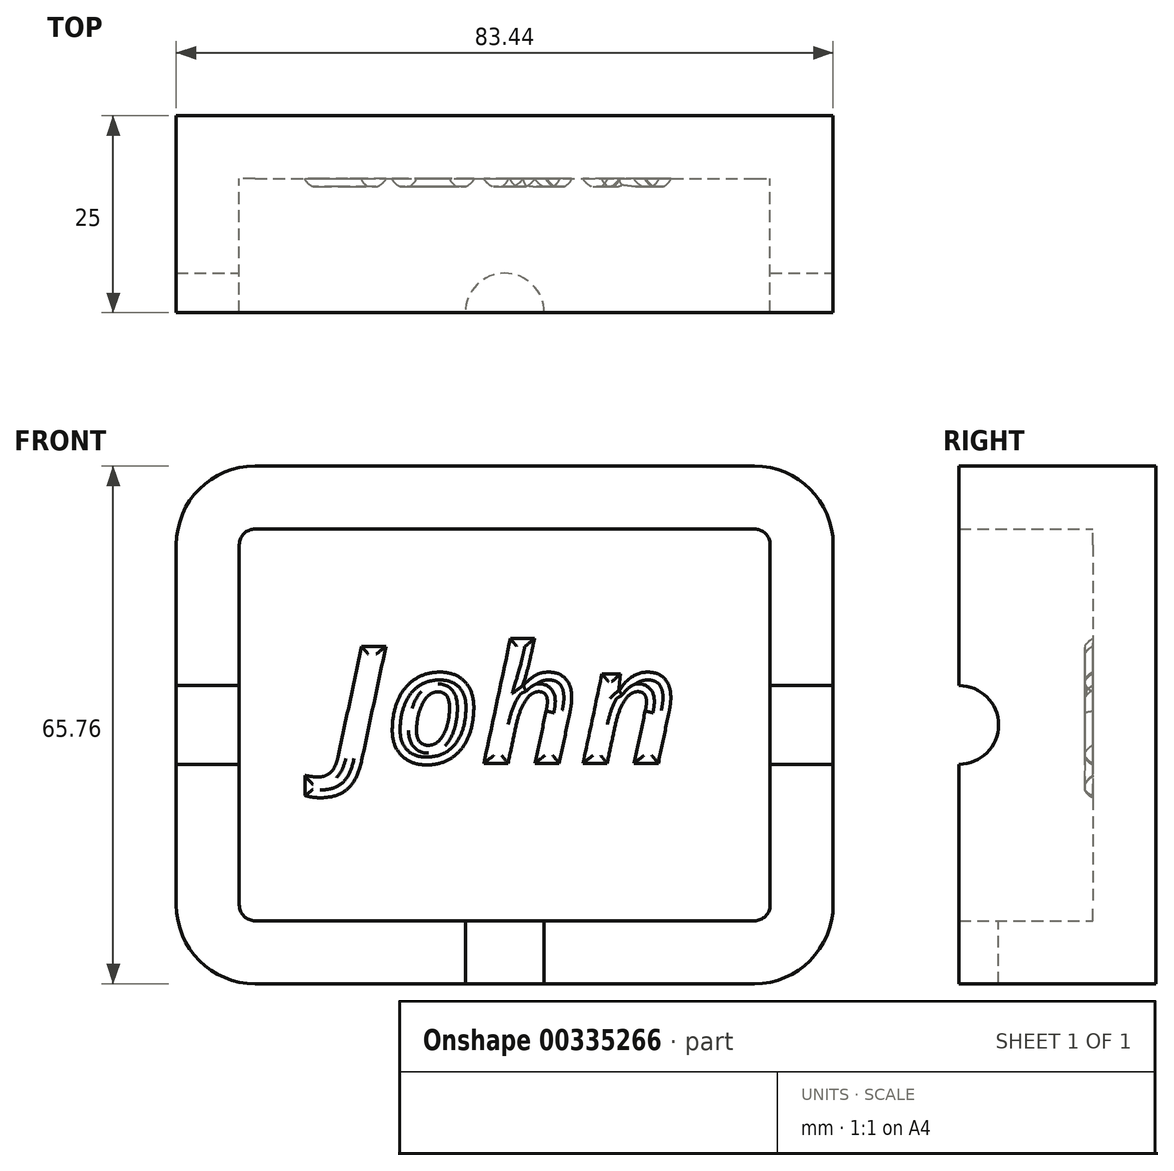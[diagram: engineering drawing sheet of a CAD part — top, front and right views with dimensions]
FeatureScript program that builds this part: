
annotation { "Feature Type Name" : "Feature", "Feature Type Description" : "" }
export const myFeature = defineFeature(function(context is Context, id is Id, definition is map)
    precondition{}
    {
        {
            var Q0;
            Q0=qCreatedBy(makeId("Front.planeOp"),FACE);
            var sketch = newSketch(context, id + "F0", { "sketchPlane" : qUnion([Q0])});
            skLineSegment(sketch, "E0.bottom", {"start": v(-52.7, 43.56) * mm, "end": v(30.74, 43.56) * mm});
            skLineSegment(sketch, "E0.top", {"start": v(-52.7, -22.2) * mm, "end": v(30.74, -22.2) * mm});
            skLineSegment(sketch, "E0.left", {"start": v(-52.7, 43.56) * mm, "end": v(-52.7, -22.2) * mm});
            skLineSegment(sketch, "E0.right", {"start": v(30.74, 43.56) * mm, "end": v(30.74, -22.2) * mm});
            skSolve(sketch);
        }
        {
            var Q0;
            Q0 = qSketchRegion(id + "F0", true);
            extrude(context, id + "F1", {"entities" : qUnion([Q0]), "depth" : 25 * mm});
        }
        {
            var Q0;
            Q0=makeQuery(id+"F1.opExtrude","SWEPT_EDGE",EDGE,{"disambiguationData":[OSD([sQuery(id+"F0.wireOp",EDGE,"E0.bottom"),sQuery(id+"F0.wireOp",EDGE,"E0.right")])]});
            var Q1;
            Q1=makeQuery(id+"F1.opExtrude","SWEPT_EDGE",EDGE,{"disambiguationData":[OSD([sQuery(id+"F0.wireOp",EDGE,"E0.top"),sQuery(id+"F0.wireOp",EDGE,"E0.right")])]});
            var Q2;
            Q2=makeQuery(id+"F1.opExtrude","SWEPT_EDGE",EDGE,{"disambiguationData":[OSD([sQuery(id+"F0.wireOp",EDGE,"E0.bottom"),sQuery(id+"F0.wireOp",EDGE,"E0.left")])]});
            var Q3;
            Q3=makeQuery(id+"F1.opExtrude","SWEPT_EDGE",EDGE,{"disambiguationData":[OSD([sQuery(id+"F0.wireOp",EDGE,"E0.top"),sQuery(id+"F0.wireOp",EDGE,"E0.left")])]});
            fillet(context, id + "F2", {"entities" : qUnion([Q0, Q1, Q2, Q3]), "radius" : 10 * mm, "tangentPropagation" : true, "allowEdgeOverflow" : false});
        }
        {
            var Q0;
            Q0=makeQuery(id+"F1.opExtrude","CAP_FACE",FACE,{"disambiguationData":[OSD([sQuery(id+"F0.wireOp",EDGE,"E0.bottom"),sQuery(id+"F0.wireOp",EDGE,"E0.top"),sQuery(id+"F0.wireOp",EDGE,"E0.left"),sQuery(id+"F0.wireOp",EDGE,"E0.right")])],"isStart":false});
            shell(context, id + "F3", {"entities" : qUnion([Q0]), "thickness" : 8 * mm});
        }
        {
            var Q0;
            Q0=makeQuery(id+"F1.opExtrude","SWEPT_FACE",FACE,{"disambiguationData":[OSD([sQuery(id+"F0.wireOp",EDGE,"E0.right")])]});
            var sketch = newSketch(context, id + "F4", { "sketchPlane" : qUnion([Q0])});
            skCircle(sketch, "E1", {"center": v(-25, 10.68) * mm, "radius": 5 * mm});
            skSolve(sketch);
        }
        {
            var Q0;
            Q0 = qSketchRegion(id + "F4", true);
            extrude(context, id + "F5", {"entities" : qUnion([Q0]), "operationType" : NewBodyOperationType.REMOVE, "oppositeDirection" : true, "depth" : 106.8 * mm});
        }
        {
            var Q0;
            Q0=qCreatedBy(makeId("Top.planeOp"),FACE);
            var sketch = newSketch(context, id + "F6", { "sketchPlane" : qUnion([Q0])});
            skCircle(sketch, "E2", {"center": v(-10.98, -25) * mm, "radius": 5 * mm});
            skSolve(sketch);
        }
        {
            var Q0;
            Q0=makeQuery(id+"F6.imprint","IMPRINT",FACE,{"disambiguationData":[TD([[makeQuery(id+"F6.imprint","IMPRINT",EDGE,{"derivedFrom":sQuery(id+"F6.wireOp",EDGE,"E2")}),1.0]])]});
            extrude(context, id + "F7", {"entities" : qUnion([Q0]), "operationType" : NewBodyOperationType.REMOVE, "oppositeDirection" : true, "depth" : 41.4 * mm});
        }
        {
            var Q0;
            Q0=qCreatedBy(makeId("Front.planeOp"),FACE);
            var sketch = newSketch(context, id + "F8", { "sketchPlane" : qUnion([Q0])});
            skText(sketch, "E3", { "text": "John", "fontName": "OpenSans-BoldItalic.ttf"});
            const initialGuessF8  = {"E3": [-0.03308, 0.0058, 1, 0, 0.015]};
            skSetInitialGuess(sketch, initialGuessF8);
            skSolve(sketch);
        }
        {
            var Q0;
            Q0 = qSketchRegion(id + "F8", true);
            extrude(context, id + "F9", {"entities" : qUnion([Q0]), "operationType" : NewBodyOperationType.ADD, "depth" : 9 * mm});
        }
        {
            var Q0;
            Q0=makeQuery(id+"F9.opExtrude","CAP_FACE",FACE,{"disambiguationData":[OSD([sQuery(id+"F8.wireOp",EDGE,"E3.sketch_text.stroke-0"),sQuery(id+"F8.wireOp",EDGE,"E3.sketch_text.stroke-1"),sQuery(id+"F8.wireOp",EDGE,"E3.sketch_text.stroke-2"),sQuery(id+"F8.wireOp",EDGE,"E3.sketch_text.stroke-3"),sQuery(id+"F8.wireOp",EDGE,"E3.sketch_text.stroke-4"),sQuery(id+"F8.wireOp",EDGE,"E3.sketch_text.stroke-5"),sQuery(id+"F8.wireOp",EDGE,"E3.sketch_text.stroke-6"),sQuery(id+"F8.wireOp",EDGE,"E3.sketch_text.stroke-7"),sQuery(id+"F8.wireOp",EDGE,"E3.sketch_text.stroke-8"),sQuery(id+"F8.wireOp",EDGE,"E3.sketch_text.stroke-9")])],"isStart":false});
            var Q1;
            Q1=makeQuery(id+"F9.opExtrude","CAP_FACE",FACE,{"disambiguationData":[OSD([sQuery(id+"F8.wireOp",EDGE,"E3.sketch_text.stroke-10"),sQuery(id+"F8.wireOp",EDGE,"E3.sketch_text.stroke-11"),sQuery(id+"F8.wireOp",EDGE,"E3.sketch_text.stroke-12"),sQuery(id+"F8.wireOp",EDGE,"E3.sketch_text.stroke-13"),sQuery(id+"F8.wireOp",EDGE,"E3.sketch_text.stroke-14"),sQuery(id+"F8.wireOp",EDGE,"E3.sketch_text.stroke-15"),sQuery(id+"F8.wireOp",EDGE,"E3.sketch_text.stroke-16"),sQuery(id+"F8.wireOp",EDGE,"E3.sketch_text.stroke-17"),sQuery(id+"F8.wireOp",EDGE,"E3.sketch_text.stroke-18"),sQuery(id+"F8.wireOp",EDGE,"E3.sketch_text.stroke-19"),sQuery(id+"F8.wireOp",EDGE,"E3.sketch_text.stroke-20"),sQuery(id+"F8.wireOp",EDGE,"E3.sketch_text.stroke-21"),sQuery(id+"F8.wireOp",EDGE,"E3.sketch_text.stroke-22"),sQuery(id+"F8.wireOp",EDGE,"E3.sketch_text.stroke-23"),sQuery(id+"F8.wireOp",EDGE,"E3.sketch_text.stroke-24"),sQuery(id+"F8.wireOp",EDGE,"E3.sketch_text.stroke-25"),sQuery(id+"F8.wireOp",EDGE,"E3.sketch_text.stroke-26"),sQuery(id+"F8.wireOp",EDGE,"E3.sketch_text.stroke-27")])],"isStart":false});
            var Q2;
            Q2=makeQuery(id+"F9.opExtrude","CAP_FACE",FACE,{"disambiguationData":[OSD([sQuery(id+"F8.wireOp",EDGE,"E3.sketch_text.stroke-28"),sQuery(id+"F8.wireOp",EDGE,"E3.sketch_text.stroke-29"),sQuery(id+"F8.wireOp",EDGE,"E3.sketch_text.stroke-30"),sQuery(id+"F8.wireOp",EDGE,"E3.sketch_text.stroke-31"),sQuery(id+"F8.wireOp",EDGE,"E3.sketch_text.stroke-32"),sQuery(id+"F8.wireOp",EDGE,"E3.sketch_text.stroke-33"),sQuery(id+"F8.wireOp",EDGE,"E3.sketch_text.stroke-34"),sQuery(id+"F8.wireOp",EDGE,"E3.sketch_text.stroke-35"),sQuery(id+"F8.wireOp",EDGE,"E3.sketch_text.stroke-36"),sQuery(id+"F8.wireOp",EDGE,"E3.sketch_text.stroke-37"),sQuery(id+"F8.wireOp",EDGE,"E3.sketch_text.stroke-38"),sQuery(id+"F8.wireOp",EDGE,"E3.sketch_text.stroke-39"),sQuery(id+"F8.wireOp",EDGE,"E3.sketch_text.stroke-40"),sQuery(id+"F8.wireOp",EDGE,"E3.sketch_text.stroke-41"),sQuery(id+"F8.wireOp",EDGE,"E3.sketch_text.stroke-42"),sQuery(id+"F8.wireOp",EDGE,"E3.sketch_text.stroke-43"),sQuery(id+"F8.wireOp",EDGE,"E3.sketch_text.stroke-44"),sQuery(id+"F8.wireOp",EDGE,"E3.sketch_text.stroke-45"),sQuery(id+"F8.wireOp",EDGE,"E3.sketch_text.stroke-46")])],"isStart":false});
            var Q3;
            Q3=makeQuery(id+"F9.opExtrude","CAP_FACE",FACE,{"disambiguationData":[OSD([sQuery(id+"F8.wireOp",EDGE,"E3.sketch_text.stroke-47"),sQuery(id+"F8.wireOp",EDGE,"E3.sketch_text.stroke-48"),sQuery(id+"F8.wireOp",EDGE,"E3.sketch_text.stroke-49"),sQuery(id+"F8.wireOp",EDGE,"E3.sketch_text.stroke-50"),sQuery(id+"F8.wireOp",EDGE,"E3.sketch_text.stroke-51"),sQuery(id+"F8.wireOp",EDGE,"E3.sketch_text.stroke-52"),sQuery(id+"F8.wireOp",EDGE,"E3.sketch_text.stroke-53"),sQuery(id+"F8.wireOp",EDGE,"E3.sketch_text.stroke-54"),sQuery(id+"F8.wireOp",EDGE,"E3.sketch_text.stroke-55"),sQuery(id+"F8.wireOp",EDGE,"E3.sketch_text.stroke-56"),sQuery(id+"F8.wireOp",EDGE,"E3.sketch_text.stroke-57"),sQuery(id+"F8.wireOp",EDGE,"E3.sketch_text.stroke-58"),sQuery(id+"F8.wireOp",EDGE,"E3.sketch_text.stroke-59"),sQuery(id+"F8.wireOp",EDGE,"E3.sketch_text.stroke-60"),sQuery(id+"F8.wireOp",EDGE,"E3.sketch_text.stroke-61"),sQuery(id+"F8.wireOp",EDGE,"E3.sketch_text.stroke-62"),sQuery(id+"F8.wireOp",EDGE,"E3.sketch_text.stroke-63")])],"isStart":false});
            var Q4;
            Q4=makeQuery(id+"F9.opExtrude","CAP_FACE",FACE,{"disambiguationData":[OSD([sQuery(id+"F8.wireOp",EDGE,"E3.sketch_text.stroke-10"),sQuery(id+"F8.wireOp",EDGE,"E3.sketch_text.stroke-11"),sQuery(id+"F8.wireOp",EDGE,"E3.sketch_text.stroke-12"),sQuery(id+"F8.wireOp",EDGE,"E3.sketch_text.stroke-13"),sQuery(id+"F8.wireOp",EDGE,"E3.sketch_text.stroke-14"),sQuery(id+"F8.wireOp",EDGE,"E3.sketch_text.stroke-15"),sQuery(id+"F8.wireOp",EDGE,"E3.sketch_text.stroke-16"),sQuery(id+"F8.wireOp",EDGE,"E3.sketch_text.stroke-17"),sQuery(id+"F8.wireOp",EDGE,"E3.sketch_text.stroke-18"),sQuery(id+"F8.wireOp",EDGE,"E3.sketch_text.stroke-19"),sQuery(id+"F8.wireOp",EDGE,"E3.sketch_text.stroke-20"),sQuery(id+"F8.wireOp",EDGE,"E3.sketch_text.stroke-21"),sQuery(id+"F8.wireOp",EDGE,"E3.sketch_text.stroke-22"),sQuery(id+"F8.wireOp",EDGE,"E3.sketch_text.stroke-23"),sQuery(id+"F8.wireOp",EDGE,"E3.sketch_text.stroke-24"),sQuery(id+"F8.wireOp",EDGE,"E3.sketch_text.stroke-25"),sQuery(id+"F8.wireOp",EDGE,"E3.sketch_text.stroke-26"),sQuery(id+"F8.wireOp",EDGE,"E3.sketch_text.stroke-27")])],"isStart":false});
            var Q5;
            Q5=makeQuery(id+"F9.opExtrude","CAP_FACE",FACE,{"disambiguationData":[OSD([sQuery(id+"F8.wireOp",EDGE,"E3.sketch_text.stroke-28"),sQuery(id+"F8.wireOp",EDGE,"E3.sketch_text.stroke-29"),sQuery(id+"F8.wireOp",EDGE,"E3.sketch_text.stroke-30"),sQuery(id+"F8.wireOp",EDGE,"E3.sketch_text.stroke-31"),sQuery(id+"F8.wireOp",EDGE,"E3.sketch_text.stroke-32"),sQuery(id+"F8.wireOp",EDGE,"E3.sketch_text.stroke-33"),sQuery(id+"F8.wireOp",EDGE,"E3.sketch_text.stroke-34"),sQuery(id+"F8.wireOp",EDGE,"E3.sketch_text.stroke-35"),sQuery(id+"F8.wireOp",EDGE,"E3.sketch_text.stroke-36"),sQuery(id+"F8.wireOp",EDGE,"E3.sketch_text.stroke-37"),sQuery(id+"F8.wireOp",EDGE,"E3.sketch_text.stroke-38"),sQuery(id+"F8.wireOp",EDGE,"E3.sketch_text.stroke-39"),sQuery(id+"F8.wireOp",EDGE,"E3.sketch_text.stroke-40"),sQuery(id+"F8.wireOp",EDGE,"E3.sketch_text.stroke-41"),sQuery(id+"F8.wireOp",EDGE,"E3.sketch_text.stroke-42"),sQuery(id+"F8.wireOp",EDGE,"E3.sketch_text.stroke-43"),sQuery(id+"F8.wireOp",EDGE,"E3.sketch_text.stroke-44"),sQuery(id+"F8.wireOp",EDGE,"E3.sketch_text.stroke-45"),sQuery(id+"F8.wireOp",EDGE,"E3.sketch_text.stroke-46")])],"isStart":false});
            var Q6;
            Q6=makeQuery(id+"F9.opExtrude","CAP_FACE",FACE,{"disambiguationData":[OSD([sQuery(id+"F8.wireOp",EDGE,"E3.sketch_text.stroke-47"),sQuery(id+"F8.wireOp",EDGE,"E3.sketch_text.stroke-48"),sQuery(id+"F8.wireOp",EDGE,"E3.sketch_text.stroke-49"),sQuery(id+"F8.wireOp",EDGE,"E3.sketch_text.stroke-50"),sQuery(id+"F8.wireOp",EDGE,"E3.sketch_text.stroke-51"),sQuery(id+"F8.wireOp",EDGE,"E3.sketch_text.stroke-52"),sQuery(id+"F8.wireOp",EDGE,"E3.sketch_text.stroke-53"),sQuery(id+"F8.wireOp",EDGE,"E3.sketch_text.stroke-54"),sQuery(id+"F8.wireOp",EDGE,"E3.sketch_text.stroke-55"),sQuery(id+"F8.wireOp",EDGE,"E3.sketch_text.stroke-56"),sQuery(id+"F8.wireOp",EDGE,"E3.sketch_text.stroke-57"),sQuery(id+"F8.wireOp",EDGE,"E3.sketch_text.stroke-58"),sQuery(id+"F8.wireOp",EDGE,"E3.sketch_text.stroke-59"),sQuery(id+"F8.wireOp",EDGE,"E3.sketch_text.stroke-60"),sQuery(id+"F8.wireOp",EDGE,"E3.sketch_text.stroke-61"),sQuery(id+"F8.wireOp",EDGE,"E3.sketch_text.stroke-62"),sQuery(id+"F8.wireOp",EDGE,"E3.sketch_text.stroke-63")])],"isStart":false});
            fillet(context, id + "F10", {"entities" : qUnion([Q0, Q1, Q2, Q3, Q4, Q5, Q6]), "radius" : 1 * mm, "rho" : 0.2, "crossSection" : FilletCrossSection.CONIC, "allowEdgeOverflow" : false});
        }
    });
